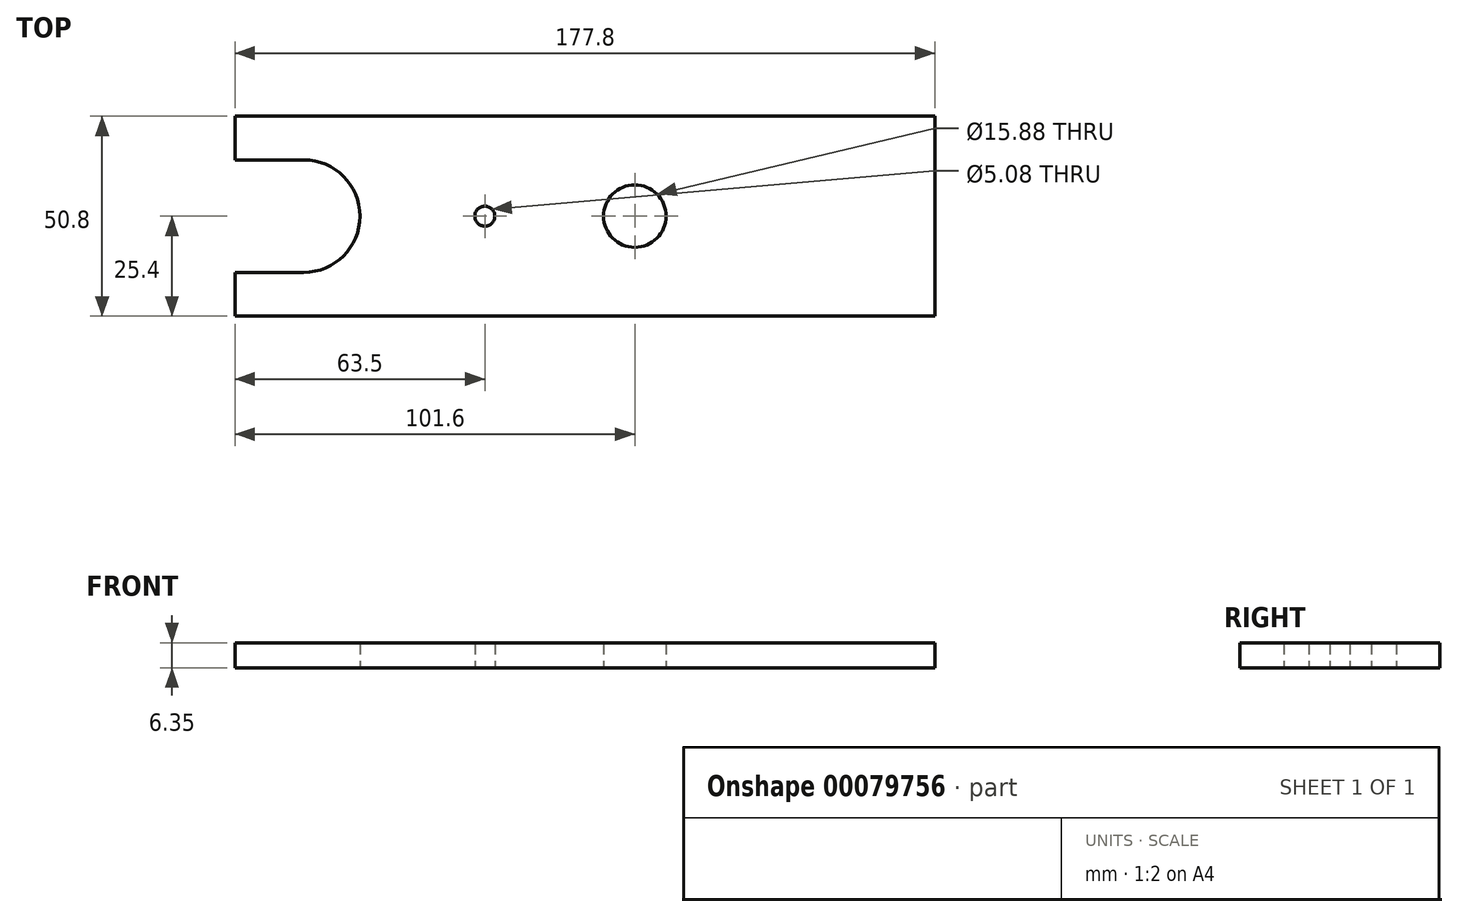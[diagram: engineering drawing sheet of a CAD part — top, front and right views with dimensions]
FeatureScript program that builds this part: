
annotation { "Feature Type Name" : "Feature", "Feature Type Description" : "" }
export const myFeature = defineFeature(function(context is Context, id is Id, definition is map)
    precondition{}
    {
        {
            var Q0;
            Q0=qCreatedBy(makeId("Top.planeOp"),FACE);
            var sketch = newSketch(context, id + "F0", { "sketchPlane" : qUnion([Q0])});
            skLineSegment(sketch, "E0.bottom", {"start": v(88.9, 25.4) * mm, "end": v(-88.9, 25.4) * mm});
            skLineSegment(sketch, "E0.top", {"start": v(88.9, -25.4) * mm, "end": v(-88.9, -25.4) * mm});
            skLineSegment(sketch, "E0.left", {"start": v(88.9, 25.4) * mm, "end": v(88.9, -25.4) * mm});
            skLineSegment(sketch, "E0.right", {"start": v(-88.9, 25.4) * mm, "end": v(-88.9, 14.29) * mm});
            skPoint(sketch, "E0.middle", {"position": v(0, 0) * mm});
            skCircle(sketch, "E1", {"center": v(12.7, 0) * mm, "radius": 7.94 * mm});
            skPoint(sketch, "E1.centerSnap0", {"position": v(-88.9, 0) * mm});
            skArc(sketch, "E2", {"start": v(-71.44, -14.29) * mm, "mid": v(-57.15, 0) * mm, "end": v(-71.44, 14.29) * mm});
            skCircle(sketch, "E3", {"center": v(-25.4, 0) * mm, "radius": 2.54 * mm});
            skLineSegment(sketch, "E4", {"start": v(-71.44, 14.29) * mm, "end": v(-88.9, 14.29) * mm});
            skLineSegment(sketch, "E5", {"start": v(-71.44, -14.29) * mm, "end": v(-88.9, -14.29) * mm});
            skLineSegment(sketch, "E6.trimOffspring", {"start": v(-88.9, -14.29) * mm, "end": v(-88.9, -25.4) * mm});
            skSolve(sketch);
        }
        {
            var Q0;
            Q0 = qSketchRegion(id + "F0", true);
            extrude(context, id + "F1", {"entities" : qUnion([Q0]), "depth" : 6.35 * mm});
        }
    });
